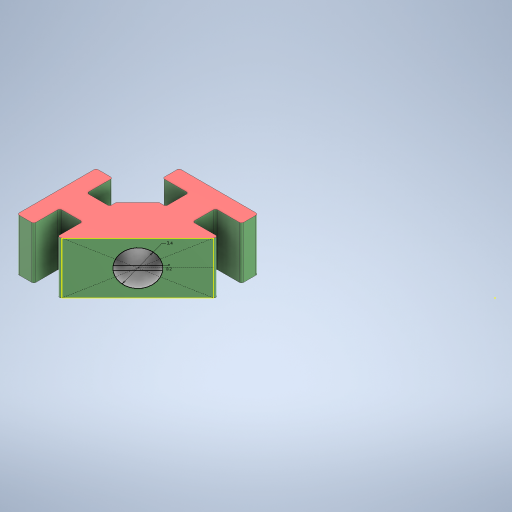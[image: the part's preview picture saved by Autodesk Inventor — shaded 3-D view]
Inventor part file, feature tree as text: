
AUTODESK INVENTOR PART (.ipt)
format: ipt  version: 2023 (Build 270158000, 158)  size: 329,728 bytes
history: native  units: mm
features: other x4, extrude x4, sketch x2, projected_geometry x1
ambient origin geometry x8: Origin, YZ Plane, XZ Plane, XY Plane, X Axis, Y Axis, Z Axis, Center Point
bodies: Body1 (feature_tree)
feature tree (11):
  other  "TmpPart3.ipt"
  sketch  "Sketch1"  dims[d0=10.0mm d1=3.4mm]
  extrude  "Extrusion1"  Depth=10.0mm
  extrude  "Extrusion2"  Depth=10.0mm TaperAngle=0.0deg
  extrude  "Extrusion3"  Depth=10.0mm TaperAngle=0.0deg
  extrude  "Extrusion4"  Depth=0.2mm
  other  "PLA2::TmpPart3.ipt"
  other  "TaggingFeature1"
  projected_geometry  "Projected Loop1"
  sketch  "Sketch2"  dims[d3=0.2mm d4=4.0mm d5=0.0mm d6=10.0mm d7=0.0mm d8=0.2mm d9=2.5mm d10=0.0mm d11=10.0mm d12=0.0mm]
  other  "PLA2"
